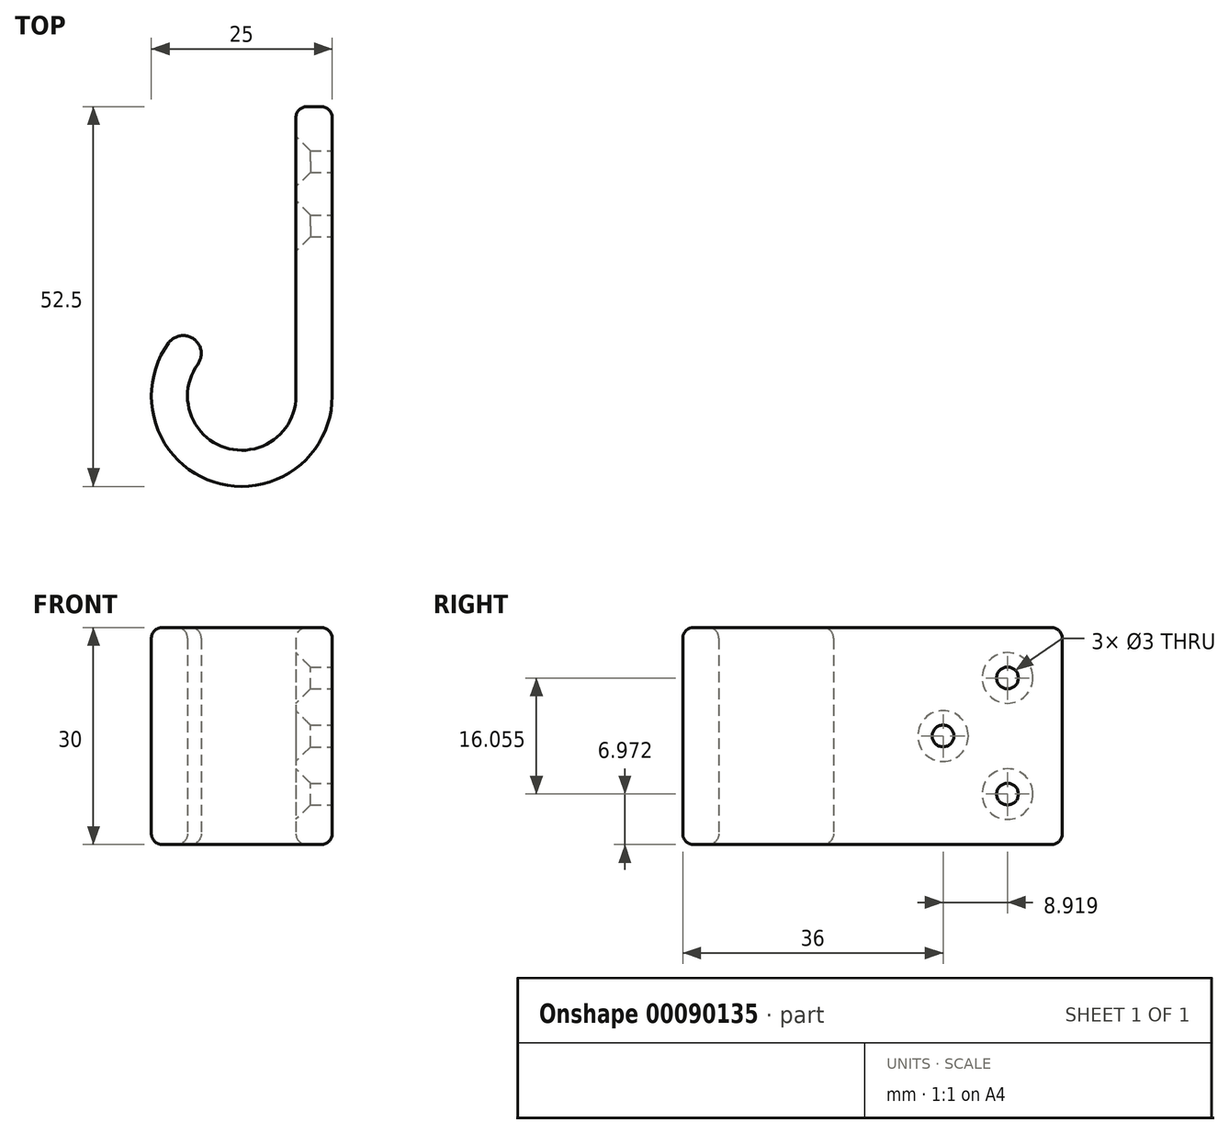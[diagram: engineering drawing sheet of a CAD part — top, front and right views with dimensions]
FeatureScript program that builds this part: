
annotation { "Feature Type Name" : "Feature", "Feature Type Description" : "" }
export const myFeature = defineFeature(function(context is Context, id is Id, definition is map)
    precondition{}
    {
        {
            var Q0;
            Q0=qCreatedBy(makeId("Top.planeOp"),FACE);
            var sketch = newSketch(context, id + "F0", { "sketchPlane" : qUnion([Q0])});
            skLineSegment(sketch, "E0", {"start": v(-5, 0) * mm, "end": v(-5, 40) * mm});
            skLineSegment(sketch, "E1", {"start": v(-5, 40) * mm, "end": v(0, 40) * mm});
            skLineSegment(sketch, "E2", {"start": v(0, 40) * mm, "end": v(0, 0) * mm});
            skArc(sketch, "E3", {"start": v(-22.63, 7.32) * mm, "mid": v(-16.35, -11.9) * mm, "end": v(0, 0) * mm});
            skArc(sketch, "E4.0", {"start": v(-18.58, 4.4) * mm, "mid": v(-14.8, -7.14) * mm, "end": v(-5, 0) * mm});
            skArc(sketch, "E5", {"start": v(-18.58, 4.4) * mm, "mid": v(-19.14, 7.89) * mm, "end": v(-22.63, 7.32) * mm});
            skLineSegment(sketch, "E6", {"start": v(-18.58, 4.4) * mm, "end": v(-22.63, 7.32) * mm, "construction": true});
            skSolve(sketch);
        }
        {
            var Q0;
            {var subQ0=sQuery(id+"F0.wireOp",EDGE,"E0");Q0=makeQuery(id+"F0.imprint","IMPRINT",FACE,{"disambiguationData":[TD([[makeQuery(id+"F0.imprint","IMPRINT",EDGE,{"derivedFrom":subQ0}),-1.0]])]});}
            var Q1;
            {var subQ3=sQuery(id+"F0.wireOp",EDGE,"E3");Q1=makeQuery(id+"F0.imprint","IMPRINT",FACE,{"disambiguationData":[TD([[makeQuery(id+"F0.imprint","IMPRINT",EDGE,{"derivedFrom":subQ3}),1.0]])]});}
            extrude(context, id + "F1", {"entities" : qUnion([Q0, Q1]), "depth" : 30 * mm});
        }
        {
            var Q0;
            Q0=makeQuery(id+"F1.opExtrude","SWEPT_EDGE",EDGE,{"disambiguationData":[OSD([sQuery(id+"F0.wireOp",EDGE,"E0"),sQuery(id+"F0.wireOp",EDGE,"E1")])]});
            var Q1;
            Q1=makeQuery(id+"F1.opExtrude","SWEPT_EDGE",EDGE,{"disambiguationData":[OSD([sQuery(id+"F0.wireOp",EDGE,"E1"),sQuery(id+"F0.wireOp",EDGE,"E2")])]});
            var Q2;
            Q2=makeQuery(id+"F1.opExtrude","CAP_EDGE",EDGE,{"disambiguationData":[OSD([sQuery(id+"F0.wireOp",EDGE,"E3")])],"isStart":true});
            var Q3;
            Q3=makeQuery(id+"F1.opExtrude","SWEPT_EDGE",EDGE,{"disambiguationData":[OSD([sQuery(id+"F0.wireOp",EDGE,"E0"),sQuery(id+"F0.wireOp",EDGE,"ypL6SIjE-rwd8-dWV7-o03M-ArZZFKEa1ukE")])]});
            var Q4;
            Q4=makeQuery(id+"F1.opExtrude","CAP_EDGE",EDGE,{"disambiguationData":[OSD([sQuery(id+"F0.wireOp",EDGE,"E3")])],"isStart":false});
            var Q5;
            Q5=makeQuery(id+"F1.opExtrude","SWEPT_EDGE",EDGE,{"disambiguationData":[OSD([sQuery(id+"F0.wireOp",EDGE,"ypL6SIjE-rwd8-dWV7-o03M-ArZZFKEa1ukE"),sQuery(id+"F0.wireOp",EDGE,"E4.0")])]});
            var Q6;
            Q6=makeQuery(id+"F1.opExtrude","CAP_EDGE",EDGE,{"disambiguationData":[OSD([sQuery(id+"F0.wireOp",EDGE,"E2")])],"isStart":true});
            var Q7;
            Q7=makeQuery(id+"F1.opExtrude","CAP_EDGE",EDGE,{"disambiguationData":[OSD([sQuery(id+"F0.wireOp",EDGE,"E4.0")])],"isStart":true});
            var Q8;
            Q8=makeQuery(id+"F1.opExtrude","CAP_EDGE",EDGE,{"disambiguationData":[OSD([sQuery(id+"F0.wireOp",EDGE,"E4.0")])],"isStart":false});
            var Q9;
            Q9=makeQuery(id+"F1.opExtrude","CAP_EDGE",EDGE,{"disambiguationData":[OSD([sQuery(id+"F0.wireOp",EDGE,"E0")])],"isStart":true});
            var Q10;
            Q10=makeQuery(id+"F1.opExtrude","CAP_EDGE",EDGE,{"disambiguationData":[OSD([sQuery(id+"F0.wireOp",EDGE,"ypL6SIjE-rwd8-dWV7-o03M-ArZZFKEa1ukE")])],"isStart":true});
            var Q11;
            Q11=makeQuery(id+"F1.opExtrude","SWEPT_EDGE",EDGE,{"disambiguationData":[OSD([sQuery(id+"F0.wireOp",EDGE,"E4.0"),sQuery(id+"F0.wireOp",EDGE,"E5")])]});
            var Q12;
            Q12=makeQuery(id+"F1.opExtrude","CAP_EDGE",EDGE,{"disambiguationData":[OSD([sQuery(id+"F0.wireOp",EDGE,"E0")])],"isStart":false});
            var Q13;
            Q13=makeQuery(id+"F1.opExtrude","CAP_EDGE",EDGE,{"disambiguationData":[OSD([sQuery(id+"F0.wireOp",EDGE,"E1")])],"isStart":true});
            var Q14;
            Q14=makeQuery(id+"F1.opExtrude","SWEPT_EDGE",EDGE,{"disambiguationData":[OSD([sQuery(id+"F0.wireOp",EDGE,"E2"),sQuery(id+"F0.wireOp",EDGE,"E3"),sQuery(id+"F0.wireOp",EDGE,"ypL6SIjE-rwd8-dWV7-o03M-ArZZFKEa1ukE")])]});
            var Q15;
            Q15=makeQuery(id+"F1.opExtrude","SWEPT_EDGE",EDGE,{"disambiguationData":[OSD([sQuery(id+"F0.wireOp",EDGE,"E3"),sQuery(id+"F0.wireOp",EDGE,"E5")])]});
            var Q16;
            Q16=makeQuery(id+"F1.opExtrude","CAP_EDGE",EDGE,{"disambiguationData":[OSD([sQuery(id+"F0.wireOp",EDGE,"E1")])],"isStart":false});
            var Q17;
            Q17=makeQuery(id+"F1.opExtrude","CAP_EDGE",EDGE,{"disambiguationData":[OSD([sQuery(id+"F0.wireOp",EDGE,"E2")])],"isStart":false});
            var Q18;
            Q18=makeQuery(id+"F1.opExtrude","CAP_EDGE",EDGE,{"disambiguationData":[OSD([sQuery(id+"F0.wireOp",EDGE,"ypL6SIjE-rwd8-dWV7-o03M-ArZZFKEa1ukE")])],"isStart":false});
            var Q19;
            Q19=makeQuery(id+"F1.opExtrude","CAP_EDGE",EDGE,{"disambiguationData":[OSD([sQuery(id+"F0.wireOp",EDGE,"E5")])],"isStart":true});
            var Q20;
            Q20=makeQuery(id+"F1.opExtrude","CAP_EDGE",EDGE,{"disambiguationData":[OSD([sQuery(id+"F0.wireOp",EDGE,"E5")])],"isStart":false});
            fillet(context, id + "F2", {"entities" : qUnion([Q0, Q1, Q2, Q3, Q4, Q5, Q6, Q7, Q8, Q9, Q10, Q11, Q12, Q13, Q14, Q15, Q16, Q17, Q18, Q19, Q20]), "radius" : 1.5 * mm, "tangentPropagation" : true, "allowEdgeOverflow" : false});
        }
        {
            var Q0;
            Q0=makeQuery(id+"F1.opExtrude","SWEPT_FACE",FACE,{"disambiguationData":[OSD([sQuery(id+"F0.wireOp",EDGE,"E0")])]});
            var sketch = newSketch(context, id + "F3", { "sketchPlane" : qUnion([Q0])});
            skCircle(sketch, "E7", {"center": v(-23.5, 15) * mm, "radius": 1.5 * mm});
            skCircle(sketch, "E8", {"center": v(-32.42, 23.03) * mm, "radius": 1.5 * mm});
            skCircle(sketch, "E9", {"center": v(-32.42, 6.97) * mm, "radius": 1.5 * mm});
            skSolve(sketch);
        }
        {
            var Q0;
            Q0 = qSketchRegion(id + "F3", true);
            extrude(context, id + "F4", {"entities" : qUnion([Q0]), "operationType" : NewBodyOperationType.REMOVE, "depth" : 25 * mm, "hasSecondDirection" : true, "secondDirectionOppositeDirection" : true, "secondDirectionDepth" : 25 * mm});
        }
        {
            var Q0;
            Q0=makeQuery(id+"F4.boolean.opBoolean","INTERSECT",EDGE,{"derivedFrom":[makeQuery(id+"F1.opExtrude","SWEPT_FACE",FACE,{"disambiguationData":[OSD([sQuery(id+"F0.wireOp",EDGE,"E0")])]}),makeQuery(id+"F4.opExtrude","SWEPT_FACE",FACE,{"disambiguationData":[OSD([sQuery(id+"F3.wireOp",EDGE,"E9")])]})]});
            var Q1;
            Q1=makeQuery(id+"F4.boolean.opBoolean","INTERSECT",EDGE,{"derivedFrom":[makeQuery(id+"F1.opExtrude","SWEPT_FACE",FACE,{"disambiguationData":[OSD([sQuery(id+"F0.wireOp",EDGE,"E0")])]}),makeQuery(id+"F4.opExtrude","SWEPT_FACE",FACE,{"disambiguationData":[OSD([sQuery(id+"F3.wireOp",EDGE,"E8")])]})]});
            var Q2;
            Q2=makeQuery(id+"F4.boolean.opBoolean","INTERSECT",EDGE,{"derivedFrom":[makeQuery(id+"F1.opExtrude","SWEPT_FACE",FACE,{"disambiguationData":[OSD([sQuery(id+"F0.wireOp",EDGE,"E0")])]}),makeQuery(id+"F4.opExtrude","SWEPT_FACE",FACE,{"disambiguationData":[OSD([sQuery(id+"F3.wireOp",EDGE,"E7")])]})]});
            chamfer(context, id + "F5", {"entities" : qUnion([Q0, Q1, Q2]), "width" : 2 * mm, "tangentPropagation" : true});
        }
    });
